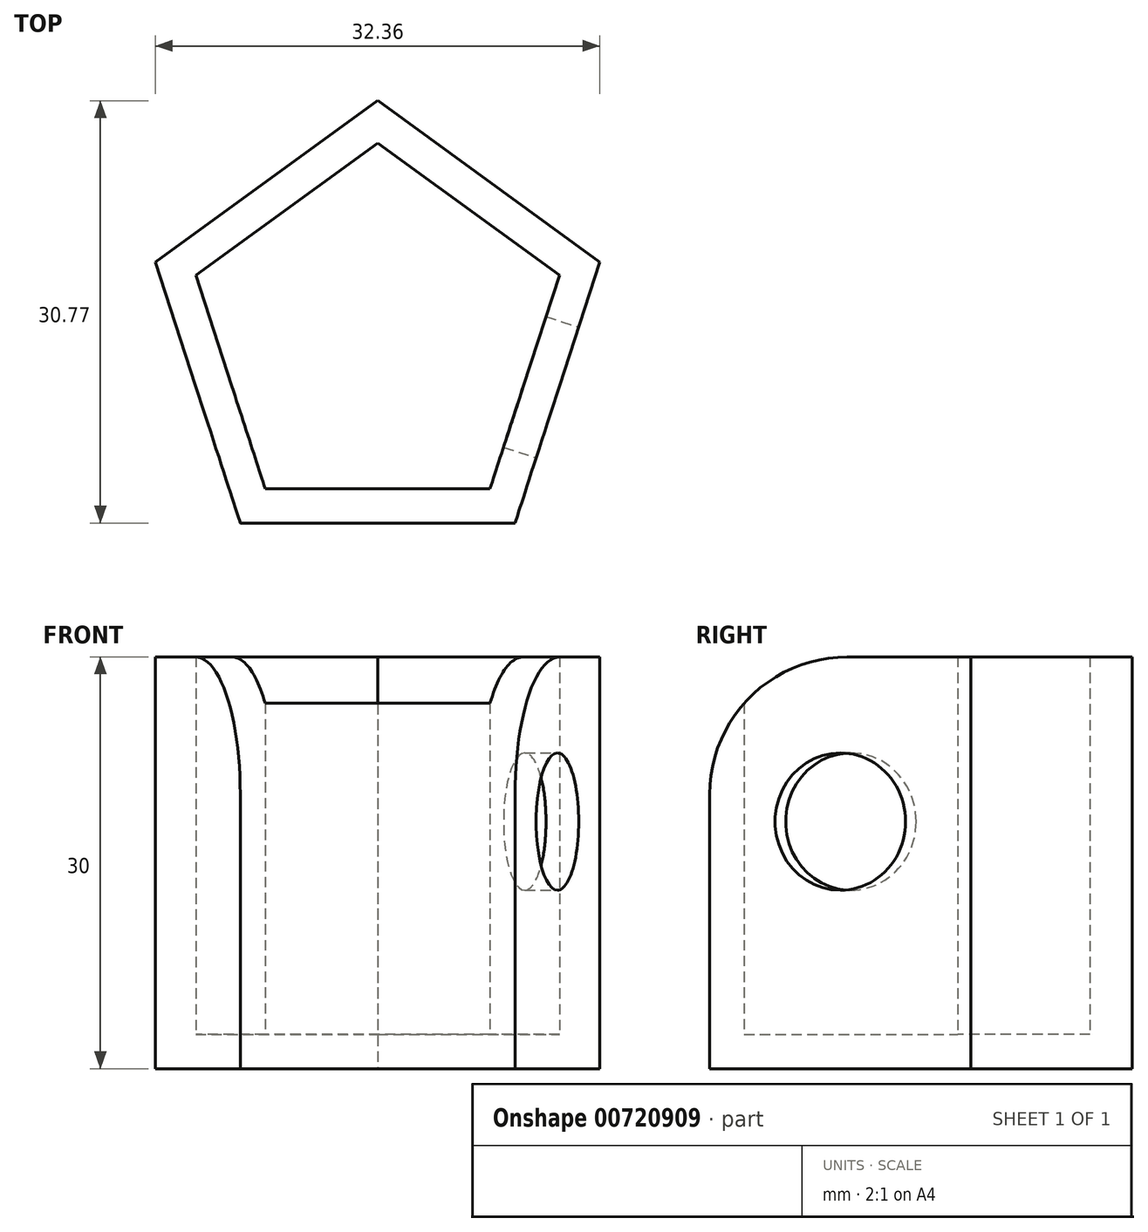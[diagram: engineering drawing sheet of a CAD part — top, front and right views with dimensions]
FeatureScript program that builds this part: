
annotation { "Feature Type Name" : "Feature", "Feature Type Description" : "" }
export const myFeature = defineFeature(function(context is Context, id is Id, definition is map)
    precondition{}
    {
        {
            var Q0;
            Q0=qCreatedBy(makeId("Top.planeOp"),FACE);
            var sketch = newSketch(context, id + "F0", { "sketchPlane" : qUnion([Q0])});
            skCircle(sketch, "E0.cCircle", {"center": v(0, 0) * mm, "radius": 13.76 * mm, "construction": true});
            skLineSegment(sketch, "E0.0", {"start": v(0, 17.01) * mm, "end": v(16.18, 5.26) * mm});
            skLineSegment(sketch, "E0.1", {"start": v(16.18, 5.26) * mm, "end": v(10, -13.76) * mm});
            skLineSegment(sketch, "E0.2", {"start": v(10, -13.76) * mm, "end": v(-10, -13.76) * mm});
            skLineSegment(sketch, "E0.3", {"start": v(-10, -13.76) * mm, "end": v(-16.18, 5.26) * mm});
            skLineSegment(sketch, "E0.4", {"start": v(-16.18, 5.26) * mm, "end": v(0, 17.01) * mm});
            skPoint(sketch, "E0.0.midPoint", {"position": v(8.1, 11.14) * mm});
            skSolve(sketch);
        }
        {
            var Q0;
            Q0=makeQuery(id+"F0.imprint","IMPRINT",FACE,{"disambiguationData":[TD([[makeQuery(id+"F0.imprint","IMPRINT",EDGE,{"derivedFrom":sQuery(id+"F0.wireOp",EDGE,"E0.0")}),-1.0]])]});
            extrude(context, id + "F1", {"entities" : qUnion([Q0]), "depth" : 30 * mm, "offsetDistance" : 25 * mm});
        }
        {
            var Q0;
            Q0=makeQuery(id+"F1.opExtrude","CAP_FACE",FACE,{"disambiguationData":[OSD([sQuery(id+"F0.wireOp",EDGE,"E0.0"),sQuery(id+"F0.wireOp",EDGE,"E0.1"),sQuery(id+"F0.wireOp",EDGE,"E0.2"),sQuery(id+"F0.wireOp",EDGE,"E0.3"),sQuery(id+"F0.wireOp",EDGE,"E0.4")])],"isStart":false});
            shell(context, id + "F2", {"entities" : qUnion([Q0]), "thickness" : 2.5 * mm});
        }
        {
            var Q0;
            Q0=makeQuery(id+"F1.opExtrude","SWEPT_FACE",FACE,{"disambiguationData":[OSD([sQuery(id+"F0.wireOp",EDGE,"E0.1")])]});
            var sketch = newSketch(context, id + "F3", { "sketchPlane" : qUnion([Q0])});
            skCircle(sketch, "E1", {"center": v(0, 18) * mm, "radius": 5 * mm});
            skPoint(sketch, "E1.centerSnap0", {"position": v(0, 0) * mm});
            skSolve(sketch);
        }
        {
            var Q0;
            Q0=makeQuery(id+"F3.imprint","IMPRINT",FACE,{"disambiguationData":[TD([[makeQuery(id+"F3.imprint","IMPRINT",EDGE,{"derivedFrom":sQuery(id+"F3.wireOp",EDGE,"E1")}),1.0]])]});
            extrude(context, id + "F4", {"entities" : qUnion([Q0]), "operationType" : NewBodyOperationType.REMOVE, "oppositeDirection" : true, "depth" : 12.6 * mm, "offsetDistance" : 25 * mm});
        }
        {
            var Q0;
            Q0=makeQuery(id+"F1.opExtrude","CAP_EDGE",EDGE,{"disambiguationData":[OSD([sQuery(id+"F0.wireOp",EDGE,"E0.2")])],"isStart":false});
            fillet(context, id + "F5", {"entities" : qUnion([Q0]), "radius" : 10 * mm, "tangentPropagation" : true, "allowEdgeOverflow" : false});
        }
    });
